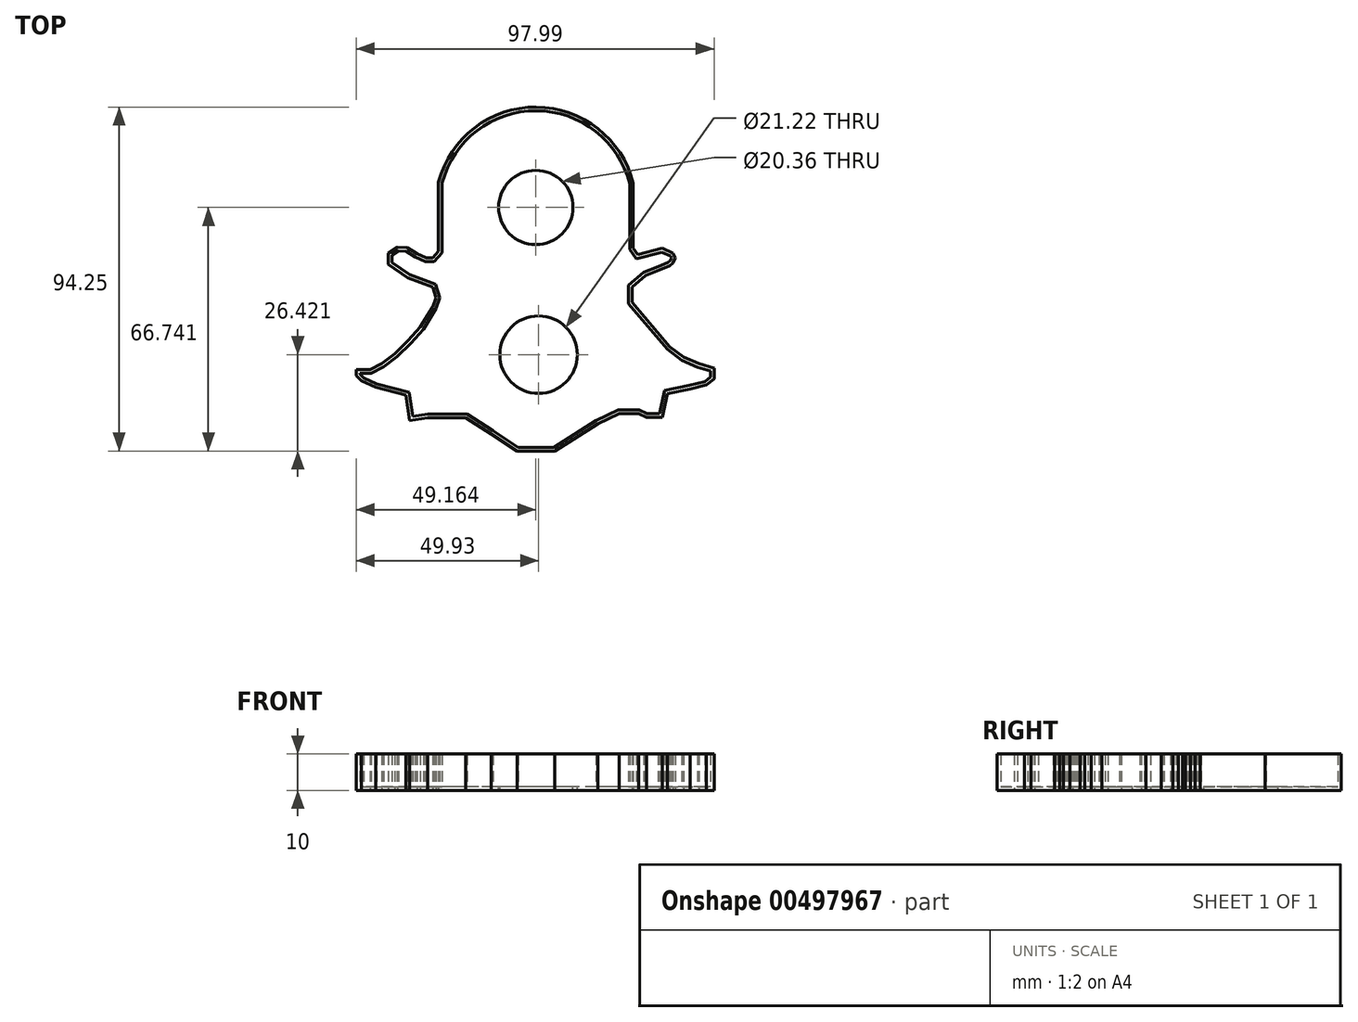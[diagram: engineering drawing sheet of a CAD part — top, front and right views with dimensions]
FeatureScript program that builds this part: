
annotation { "Feature Type Name" : "Feature", "Feature Type Description" : "" }
export const myFeature = defineFeature(function(context is Context, id is Id, definition is map)
    precondition{}
    {
        {
            var Q0;
            Q0=qCreatedBy(makeId("Top.planeOp"),FACE);
            var sketch = newSketch(context, id + "F0", { "sketchPlane" : qUnion([Q0])});
            skArc(sketch, "E0", {"start": v(25.94, 28.42) * mm, "mid": v(-0.62, 49.32) * mm, "end": v(-27.4, 28.71) * mm});
            skLineSegment(sketch, "E1", {"start": v(-27.4, 28.71) * mm, "end": v(-27.4, 9.76) * mm});
            skLineSegment(sketch, "E2", {"start": v(25.94, 28.42) * mm, "end": v(25.94, 10.64) * mm});
            skLineSegment(sketch, "E3", {"start": v(25.94, 10.64) * mm, "end": v(27.19, 8.93) * mm});
            skLineSegment(sketch, "E4", {"start": v(27.19, 8.93) * mm, "end": v(33.91, 10.64) * mm});
            skLineSegment(sketch, "E5", {"start": v(33.91, 10.64) * mm, "end": v(36.85, 9.25) * mm});
            skLineSegment(sketch, "E6", {"start": v(36.85, 9.25) * mm, "end": v(37.5, 8) * mm});
            skLineSegment(sketch, "E7", {"start": v(37.5, 8) * mm, "end": v(36.85, 6.56) * mm});
            skLineSegment(sketch, "E8", {"start": v(36.85, 6.56) * mm, "end": v(35.92, 5.83) * mm});
            skLineSegment(sketch, "E9", {"start": v(35.92, 5.83) * mm, "end": v(33.15, 4.66) * mm});
            skLineSegment(sketch, "E10", {"start": v(33.15, 4.66) * mm, "end": v(29.36, 3.18) * mm});
            skLineSegment(sketch, "E11", {"start": v(29.36, 3.18) * mm, "end": v(25.62, 0) * mm});
            skLineSegment(sketch, "E12", {"start": v(25.62, 0) * mm, "end": v(25.62, -4.17) * mm});
            skLineSegment(sketch, "E13", {"start": v(25.62, -4.17) * mm, "end": v(28.1, -7.1) * mm});
            skLineSegment(sketch, "E14", {"start": v(28.1, -7.1) * mm, "end": v(31.62, -11.25) * mm});
            skLineSegment(sketch, "E15", {"start": v(31.62, -11.25) * mm, "end": v(35.92, -16.32) * mm});
            skLineSegment(sketch, "E16", {"start": v(35.92, -16.32) * mm, "end": v(39.73, -19.2) * mm});
            skLineSegment(sketch, "E17", {"start": v(39.73, -19.2) * mm, "end": v(43.9, -21) * mm});
            skLineSegment(sketch, "E18", {"start": v(43.9, -21) * mm, "end": v(48.06, -22.27) * mm});
            skLineSegment(sketch, "E19", {"start": v(48.06, -22.27) * mm, "end": v(48.06, -25.08) * mm});
            skLineSegment(sketch, "E20", {"start": v(48.06, -25.08) * mm, "end": v(45.98, -26.84) * mm});
            skLineSegment(sketch, "E21", {"start": v(45.98, -26.84) * mm, "end": v(41.48, -27.89) * mm});
            skLineSegment(sketch, "E22", {"start": v(41.48, -27.89) * mm, "end": v(35.35, -29.2) * mm});
            skLineSegment(sketch, "E23", {"start": v(35.35, -29.2) * mm, "end": v(33.91, -35.67) * mm});
            skLineSegment(sketch, "E24", {"start": v(33.91, -35.67) * mm, "end": v(29.54, -35.67) * mm});
            skLineSegment(sketch, "E25", {"start": v(29.54, -35.67) * mm, "end": v(27.36, -34.68) * mm});
            skLineSegment(sketch, "E26", {"start": v(27.36, -34.68) * mm, "end": v(22.08, -34.68) * mm});
            skLineSegment(sketch, "E27", {"start": v(22.08, -34.68) * mm, "end": v(16.27, -37.45) * mm});
            skLineSegment(sketch, "E28", {"start": v(16.27, -37.45) * mm, "end": v(11.26, -40.62) * mm});
            skLineSegment(sketch, "E29", {"start": v(11.26, -40.62) * mm, "end": v(4.43, -44.93) * mm});
            skLineSegment(sketch, "E30", {"start": v(4.43, -44.93) * mm, "end": v(-5.9, -44.93) * mm});
            skLineSegment(sketch, "E31", {"start": v(-5.9, -44.93) * mm, "end": v(-13, -40.22) * mm});
            skLineSegment(sketch, "E32", {"start": v(-13, -40.22) * mm, "end": v(-19.9, -35.85) * mm});
            skLineSegment(sketch, "E33", {"start": v(-19.9, -35.85) * mm, "end": v(-30.35, -35.85) * mm});
            skLineSegment(sketch, "E34", {"start": v(-30.35, -35.85) * mm, "end": v(-35.32, -36.56) * mm});
            skLineSegment(sketch, "E35", {"start": v(-35.32, -36.56) * mm, "end": v(-36.32, -29.58) * mm});
            skLineSegment(sketch, "E36", {"start": v(-36.32, -29.58) * mm, "end": v(-44.65, -27.44) * mm});
            skLineSegment(sketch, "E37", {"start": v(-44.65, -27.44) * mm, "end": v(-48.5, -25.71) * mm});
            skLineSegment(sketch, "E38", {"start": v(-48.5, -25.71) * mm, "end": v(-49.93, -24.3) * mm});
            skLineSegment(sketch, "E39", {"start": v(-49.93, -24.3) * mm, "end": v(-49.93, -22.57) * mm});
            skLineSegment(sketch, "E40", {"start": v(-49.93, -22.57) * mm, "end": v(-46.07, -22.57) * mm});
            skLineSegment(sketch, "E41", {"start": v(-46.07, -22.57) * mm, "end": v(-42.93, -20.94) * mm});
            skLineSegment(sketch, "E42", {"start": v(-42.93, -20.94) * mm, "end": v(-39.38, -18.3) * mm});
            skLineSegment(sketch, "E43", {"start": v(-39.38, -18.3) * mm, "end": v(-35.73, -14.66) * mm});
            skLineSegment(sketch, "E44", {"start": v(-35.73, -14.66) * mm, "end": v(-32.38, -10.9) * mm});
            skLineSegment(sketch, "E45", {"start": v(-32.38, -10.9) * mm, "end": v(-29.03, -5.43) * mm});
            skLineSegment(sketch, "E46", {"start": v(-29.03, -5.43) * mm, "end": v(-28.12, -2.9) * mm});
            skLineSegment(sketch, "E47", {"start": v(-28.12, -2.9) * mm, "end": v(-29.03, 0) * mm});
            skLineSegment(sketch, "E48", {"start": v(-29.03, 0) * mm, "end": v(-35.8, 2.48) * mm});
            skLineSegment(sketch, "E49", {"start": v(-35.8, 2.48) * mm, "end": v(-41.18, 6.22) * mm});
            skLineSegment(sketch, "E50", {"start": v(-41.18, 6.22) * mm, "end": v(-41.18, 9.29) * mm});
            skLineSegment(sketch, "E51", {"start": v(-41.18, 9.29) * mm, "end": v(-38.66, 10.94) * mm});
            skLineSegment(sketch, "E52", {"start": v(-38.66, 10.94) * mm, "end": v(-35.92, 10.83) * mm});
            skLineSegment(sketch, "E53", {"start": v(-35.92, 10.83) * mm, "end": v(-33.28, 9.18) * mm});
            skLineSegment(sketch, "E54", {"start": v(-33.28, 9.18) * mm, "end": v(-30.76, 7.97) * mm});
            skLineSegment(sketch, "E55", {"start": v(-30.76, 7.97) * mm, "end": v(-29, 7.97) * mm});
            skLineSegment(sketch, "E56", {"start": v(-29, 7.97) * mm, "end": v(-27.4, 9.76) * mm});
            skSolve(sketch);
        }
        {
            var Q0;
            Q0=makeQuery(id+"F0.imprint","IMPRINT",FACE,{"disambiguationData":[TD([[makeQuery(id+"F0.imprint","IMPRINT",EDGE,{"derivedFrom":sQuery(id+"F0.wireOp",EDGE,"E0")}),1.0]])]});
            extrude(context, id + "F1", {"entities" : qUnion([Q0]), "depth" : 10 * mm});
        }
        {
            var Q0;
            Q0=makeQuery(id+"F1.opExtrude","CAP_FACE",FACE,{"disambiguationData":[OSD([sQuery(id+"F0.wireOp",EDGE,"E0"),sQuery(id+"F0.wireOp",EDGE,"E1"),sQuery(id+"F0.wireOp",EDGE,"E2"),sQuery(id+"F0.wireOp",EDGE,"E3"),sQuery(id+"F0.wireOp",EDGE,"E4"),sQuery(id+"F0.wireOp",EDGE,"E5"),sQuery(id+"F0.wireOp",EDGE,"E6"),sQuery(id+"F0.wireOp",EDGE,"E7"),sQuery(id+"F0.wireOp",EDGE,"E8"),sQuery(id+"F0.wireOp",EDGE,"E9"),sQuery(id+"F0.wireOp",EDGE,"E10"),sQuery(id+"F0.wireOp",EDGE,"E11"),sQuery(id+"F0.wireOp",EDGE,"E12"),sQuery(id+"F0.wireOp",EDGE,"E13"),sQuery(id+"F0.wireOp",EDGE,"E14"),sQuery(id+"F0.wireOp",EDGE,"E15"),sQuery(id+"F0.wireOp",EDGE,"E16"),sQuery(id+"F0.wireOp",EDGE,"E17"),sQuery(id+"F0.wireOp",EDGE,"E18"),sQuery(id+"F0.wireOp",EDGE,"E19"),sQuery(id+"F0.wireOp",EDGE,"E20"),sQuery(id+"F0.wireOp",EDGE,"E21"),sQuery(id+"F0.wireOp",EDGE,"E22"),sQuery(id+"F0.wireOp",EDGE,"E23"),sQuery(id+"F0.wireOp",EDGE,"E24"),sQuery(id+"F0.wireOp",EDGE,"E25"),sQuery(id+"F0.wireOp",EDGE,"E26"),sQuery(id+"F0.wireOp",EDGE,"E27"),sQuery(id+"F0.wireOp",EDGE,"E28"),sQuery(id+"F0.wireOp",EDGE,"E29"),sQuery(id+"F0.wireOp",EDGE,"E30"),sQuery(id+"F0.wireOp",EDGE,"E31"),sQuery(id+"F0.wireOp",EDGE,"E32"),sQuery(id+"F0.wireOp",EDGE,"E33"),sQuery(id+"F0.wireOp",EDGE,"E34"),sQuery(id+"F0.wireOp",EDGE,"E35"),sQuery(id+"F0.wireOp",EDGE,"E36"),sQuery(id+"F0.wireOp",EDGE,"E37"),sQuery(id+"F0.wireOp",EDGE,"E38"),sQuery(id+"F0.wireOp",EDGE,"E39"),sQuery(id+"F0.wireOp",EDGE,"E40"),sQuery(id+"F0.wireOp",EDGE,"E41"),sQuery(id+"F0.wireOp",EDGE,"E42"),sQuery(id+"F0.wireOp",EDGE,"E43"),sQuery(id+"F0.wireOp",EDGE,"E44"),sQuery(id+"F0.wireOp",EDGE,"E45"),sQuery(id+"F0.wireOp",EDGE,"E46"),sQuery(id+"F0.wireOp",EDGE,"E47"),sQuery(id+"F0.wireOp",EDGE,"E48"),sQuery(id+"F0.wireOp",EDGE,"E49"),sQuery(id+"F0.wireOp",EDGE,"E50"),sQuery(id+"F0.wireOp",EDGE,"E51"),sQuery(id+"F0.wireOp",EDGE,"E52"),sQuery(id+"F0.wireOp",EDGE,"E53"),sQuery(id+"F0.wireOp",EDGE,"E54"),sQuery(id+"F0.wireOp",EDGE,"E55"),sQuery(id+"F0.wireOp",EDGE,"E56")])],"isStart":false});
            shell(context, id + "F2", {"entities" : qUnion([Q0]), "thickness" : 1 * mm});
        }
        {
            var Q0;
            Q0=makeQuery(id+"F2.opShell","OFFSET_FACE",FACE,{"disambiguationData":[OSD([sQuery(id+"F0.wireOp",EDGE,"E0"),sQuery(id+"F0.wireOp",EDGE,"E1"),sQuery(id+"F0.wireOp",EDGE,"E2"),sQuery(id+"F0.wireOp",EDGE,"E3"),sQuery(id+"F0.wireOp",EDGE,"E4"),sQuery(id+"F0.wireOp",EDGE,"E5"),sQuery(id+"F0.wireOp",EDGE,"E6"),sQuery(id+"F0.wireOp",EDGE,"E7"),sQuery(id+"F0.wireOp",EDGE,"E8"),sQuery(id+"F0.wireOp",EDGE,"E9"),sQuery(id+"F0.wireOp",EDGE,"E10"),sQuery(id+"F0.wireOp",EDGE,"E11"),sQuery(id+"F0.wireOp",EDGE,"E12"),sQuery(id+"F0.wireOp",EDGE,"E13"),sQuery(id+"F0.wireOp",EDGE,"E14"),sQuery(id+"F0.wireOp",EDGE,"E15"),sQuery(id+"F0.wireOp",EDGE,"E16"),sQuery(id+"F0.wireOp",EDGE,"E17"),sQuery(id+"F0.wireOp",EDGE,"E18"),sQuery(id+"F0.wireOp",EDGE,"E19"),sQuery(id+"F0.wireOp",EDGE,"E20"),sQuery(id+"F0.wireOp",EDGE,"E21"),sQuery(id+"F0.wireOp",EDGE,"E22"),sQuery(id+"F0.wireOp",EDGE,"E23"),sQuery(id+"F0.wireOp",EDGE,"E24"),sQuery(id+"F0.wireOp",EDGE,"E25"),sQuery(id+"F0.wireOp",EDGE,"E26"),sQuery(id+"F0.wireOp",EDGE,"E27"),sQuery(id+"F0.wireOp",EDGE,"E28"),sQuery(id+"F0.wireOp",EDGE,"E29"),sQuery(id+"F0.wireOp",EDGE,"E30"),sQuery(id+"F0.wireOp",EDGE,"E31"),sQuery(id+"F0.wireOp",EDGE,"E32"),sQuery(id+"F0.wireOp",EDGE,"E33"),sQuery(id+"F0.wireOp",EDGE,"E34"),sQuery(id+"F0.wireOp",EDGE,"E35"),sQuery(id+"F0.wireOp",EDGE,"E36"),sQuery(id+"F0.wireOp",EDGE,"E37"),sQuery(id+"F0.wireOp",EDGE,"E38"),sQuery(id+"F0.wireOp",EDGE,"E39"),sQuery(id+"F0.wireOp",EDGE,"E40"),sQuery(id+"F0.wireOp",EDGE,"E41"),sQuery(id+"F0.wireOp",EDGE,"E42"),sQuery(id+"F0.wireOp",EDGE,"E43"),sQuery(id+"F0.wireOp",EDGE,"E44"),sQuery(id+"F0.wireOp",EDGE,"E45"),sQuery(id+"F0.wireOp",EDGE,"E46"),sQuery(id+"F0.wireOp",EDGE,"E47"),sQuery(id+"F0.wireOp",EDGE,"E48"),sQuery(id+"F0.wireOp",EDGE,"E49"),sQuery(id+"F0.wireOp",EDGE,"E50"),sQuery(id+"F0.wireOp",EDGE,"E51"),sQuery(id+"F0.wireOp",EDGE,"E52"),sQuery(id+"F0.wireOp",EDGE,"E53"),sQuery(id+"F0.wireOp",EDGE,"E54"),sQuery(id+"F0.wireOp",EDGE,"E55"),sQuery(id+"F0.wireOp",EDGE,"E56")])]});
            var sketch = newSketch(context, id + "F3", { "sketchPlane" : qUnion([Q0])});
            skCircle(sketch, "E57", {"center": v(-0.77, 21.81) * mm, "radius": 10.18 * mm});
            skCircle(sketch, "E58", {"center": v(0, -18.5) * mm, "radius": 10.6 * mm});
            skSolve(sketch);
        }
        {
            var Q0;
            Q0=makeQuery(id+"F3.imprint","IMPRINT",FACE,{"disambiguationData":[TD([[makeQuery(id+"F3.imprint","IMPRINT",EDGE,{"derivedFrom":sQuery(id+"F3.wireOp",EDGE,"E57")}),1.0]])]});
            var Q1;
            Q1=makeQuery(id+"F3.imprint","IMPRINT",FACE,{"disambiguationData":[TD([[makeQuery(id+"F3.imprint","IMPRINT",EDGE,{"derivedFrom":sQuery(id+"F3.wireOp",EDGE,"E58")}),1.0]])]});
            extrude(context, id + "F4", {"entities" : qUnion([Q0, Q1]), "operationType" : NewBodyOperationType.REMOVE, "endBound" : BoundingType.THROUGH_ALL, "oppositeDirection" : true, "depth" : 25 * mm});
        }
    });
